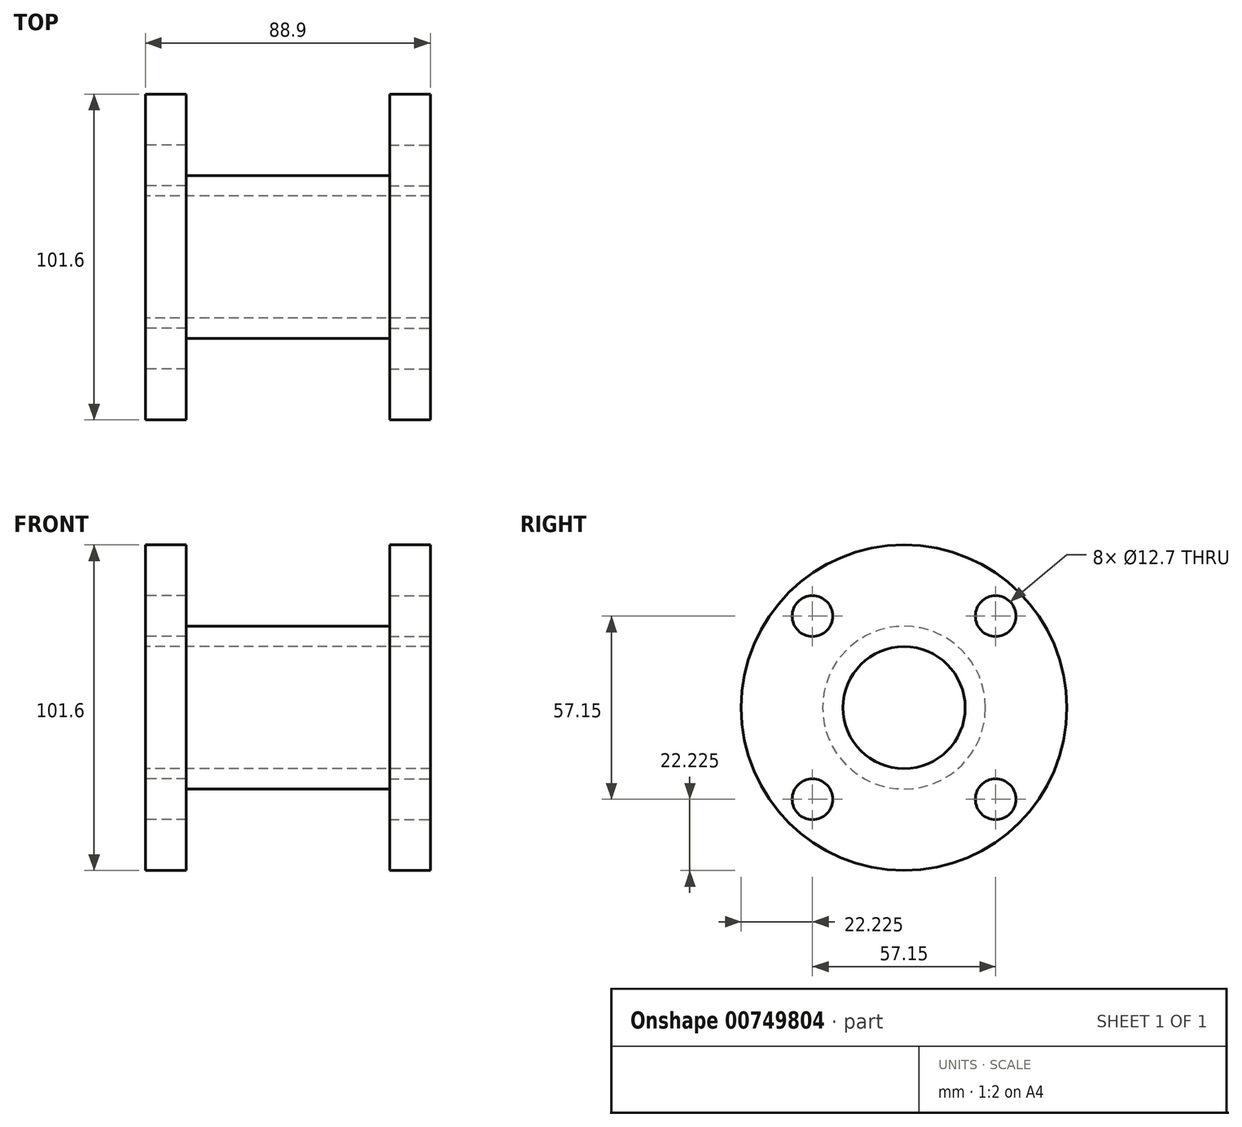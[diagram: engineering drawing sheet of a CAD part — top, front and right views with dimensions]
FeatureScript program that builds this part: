
annotation { "Feature Type Name" : "Feature", "Feature Type Description" : "" }
export const myFeature = defineFeature(function(context is Context, id is Id, definition is map)
    precondition{}
    {
        {
            var Q0;
            Q0=qCreatedBy(makeId("Right.planeOp"),FACE);
            var sketch = newSketch(context, id + "F0", { "sketchPlane" : qUnion([Q0])});
            skCircle(sketch, "E0", {"center": v(0, 0) * mm, "radius": 50.8 * mm});
            skCircle(sketch, "E1", {"center": v(0, 0) * mm, "radius": 19.05 * mm});
            skCircle(sketch, "E2", {"center": v(-28.58, 28.58) * mm, "radius": 6.35 * mm});
            skCircle(sketch, "E3", {"center": v(28.58, 28.58) * mm, "radius": 6.35 * mm});
            skCircle(sketch, "E4", {"center": v(28.58, -28.57) * mm, "radius": 6.35 * mm});
            skCircle(sketch, "E5", {"center": v(-28.57, -28.58) * mm, "radius": 6.35 * mm});
            skLineSegment(sketch, "E6", {"start": v(0, 50.8) * mm, "end": v(0, -50.8) * mm, "construction": true});
            skLineSegment(sketch, "E7", {"start": v(-50.8, 0) * mm, "end": v(50.8, 0) * mm, "construction": true});
            skLineSegment(sketch, "E8", {"start": v(-28.58, 28.58) * mm, "end": v(-28.57, 0) * mm, "construction": true});
            skLineSegment(sketch, "E9", {"start": v(-28.58, 0) * mm, "end": v(-28.57, -28.58) * mm, "construction": true});
            skLineSegment(sketch, "E10", {"start": v(28.58, -28.58) * mm, "end": v(0, -28.58) * mm, "construction": true});
            skCircle(sketch, "E11", {"center": v(0, 0) * mm, "radius": 25.4 * mm});
            skSolve(sketch);
        }
        {
            var Q0;
            Q0 = qSketchRegion(id + "F0", true);
            extrude(context, id + "F1", {"entities" : qUnion([Q0]), "depth" : 12.7 * mm, "offsetDistance" : 25.4 * mm});
        }
        {
            var Q0;
            Q0=makeQuery(id+"F0.imprint","IMPRINT",FACE,{"disambiguationData":[TD([[makeQuery(id+"F0.imprint","IMPRINT",EDGE,{"derivedFrom":sQuery(id+"F0.wireOp",EDGE,"E1")}),-1.0]])]});
            extrude(context, id + "F2", {"entities" : qUnion([Q0]), "operationType" : NewBodyOperationType.ADD, "depth" : 88.9 * mm, "offsetDistance" : 25.4 * mm});
        }
        {
            var Q0;
            Q0=makeQuery(id+"F2.opExtrude","CAP_FACE",FACE,{"disambiguationData":[OSD([sQuery(id+"F0.wireOp",EDGE,"E1"),sQuery(id+"F0.wireOp",EDGE,"E11")])],"isStart":false});
            var sketch = newSketch(context, id + "F3", { "sketchPlane" : qUnion([Q0])});
            skCircle(sketch, "E12", {"center": v(0, 0) * mm, "radius": 50.8 * mm});
            skCircle(sketch, "E13", {"center": v(0, 0) * mm, "radius": 19.05 * mm});
            skCircle(sketch, "E14", {"center": v(-28.57, 28.58) * mm, "radius": 6.35 * mm});
            skCircle(sketch, "E15", {"center": v(28.58, 28.58) * mm, "radius": 6.35 * mm});
            skCircle(sketch, "E16", {"center": v(28.58, -28.58) * mm, "radius": 6.35 * mm});
            skCircle(sketch, "E17", {"center": v(-28.57, -28.58) * mm, "radius": 6.35 * mm});
            skLineSegment(sketch, "E18", {"start": v(0, 50.8) * mm, "end": v(0, -50.8) * mm, "construction": true});
            skLineSegment(sketch, "E19", {"start": v(-50.8, 0) * mm, "end": v(50.8, 0) * mm, "construction": true});
            skLineSegment(sketch, "E20", {"start": v(-28.57, 28.58) * mm, "end": v(-28.57, 0) * mm, "construction": true});
            skLineSegment(sketch, "E21", {"start": v(-28.57, 0) * mm, "end": v(-28.57, -28.58) * mm, "construction": true});
            skLineSegment(sketch, "E22", {"start": v(28.58, -28.57) * mm, "end": v(0, -28.58) * mm, "construction": true});
            skCircle(sketch, "E23", {"center": v(0, 0) * mm, "radius": 25.4 * mm});
            skSolve(sketch);
        }
        {
            var Q0;
            Q0 = qSketchRegion(id + "F3", true);
            extrude(context, id + "F4", {"entities" : qUnion([Q0]), "operationType" : NewBodyOperationType.ADD, "oppositeDirection" : true, "depth" : 12.7 * mm, "offsetDistance" : 25.4 * mm});
        }
    });
